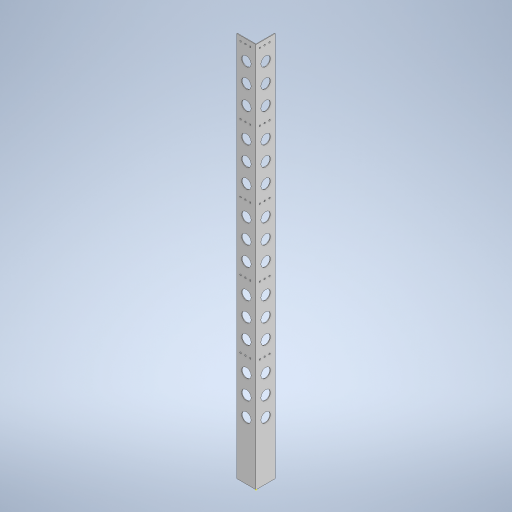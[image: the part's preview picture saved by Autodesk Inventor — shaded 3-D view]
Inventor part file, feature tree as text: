
AUTODESK INVENTOR PART (.ipt)
format: ipt  version: 2024 (Build 280153000, 153)  size: 399,872 bytes
history: native  units: mm
features: sketch x4, extrude x3
ambient origin geometry x8: Origin, YZ Plane, XZ Plane, XY Plane, X Axis, Y Axis, Z Axis, Center Point
bodies: Body1 (feature_tree)
feature tree (7):
  extrude  "Extrusión6"  Depth=100.0mm
  sketch  "Boceto9"  dims[d48=3.0mm d49=2000.0mm d50=0.0mm]
  extrude  "Extrusión10"  Depth=2000.0mm TaperAngle=0.0deg
  extrude  "Extrusión11"  Depth=10.0mm
  sketch  "Boceto6"  dims[d46=100.0mm d47=100.0mm]
  sketch  "Boceto12"  dims[d113=50.0mm d114=50.0mm d116=350.0mm d117=10.0mm d119=10.0mm]
  sketch  "Boceto13"  dims[d121=50.0mm d122=50.0mm d123=50.0mm d124=30.0mm d126=100.0mm d127=10.0mm d129=10.0mm d135=8.0mm d136=8.0mm d137=8.0mm d138=25.0mm d139=25.0mm d140=25.0mm d141=20.0mm d142=30.0mm d143=25.0mm d144=25.0mm d145=50.0mm d147=350.0mm d148=10.0mm d150=10.0mm d152=2000.0mm d153=0.0mm d155=50.0mm d157=10.0mm d159=30.0mm d161=10.0mm d163=50.0mm d165=10.0mm d166=50.0mm d167=350.0mm d168=50.0mm d169=50.0mm d170=50.0mm d171=100.0mm d172=8.0mm d173=8.0mm d174=8.0mm d175=25.0mm d176=25.0mm d177=25.0mm d178=20.0mm d179=30.0mm d180=25.0mm d181=25.0mm d182=350.0mm d183=10.0mm d184=10.0mm d185=10.0mm d186=0.0mm d187=0.0mm d188=0.0mm d189=2000.0mm d190=0.0mm d2=0.5mm d3=0.872665mm d4=0.5mm d5=0.872665mm]
